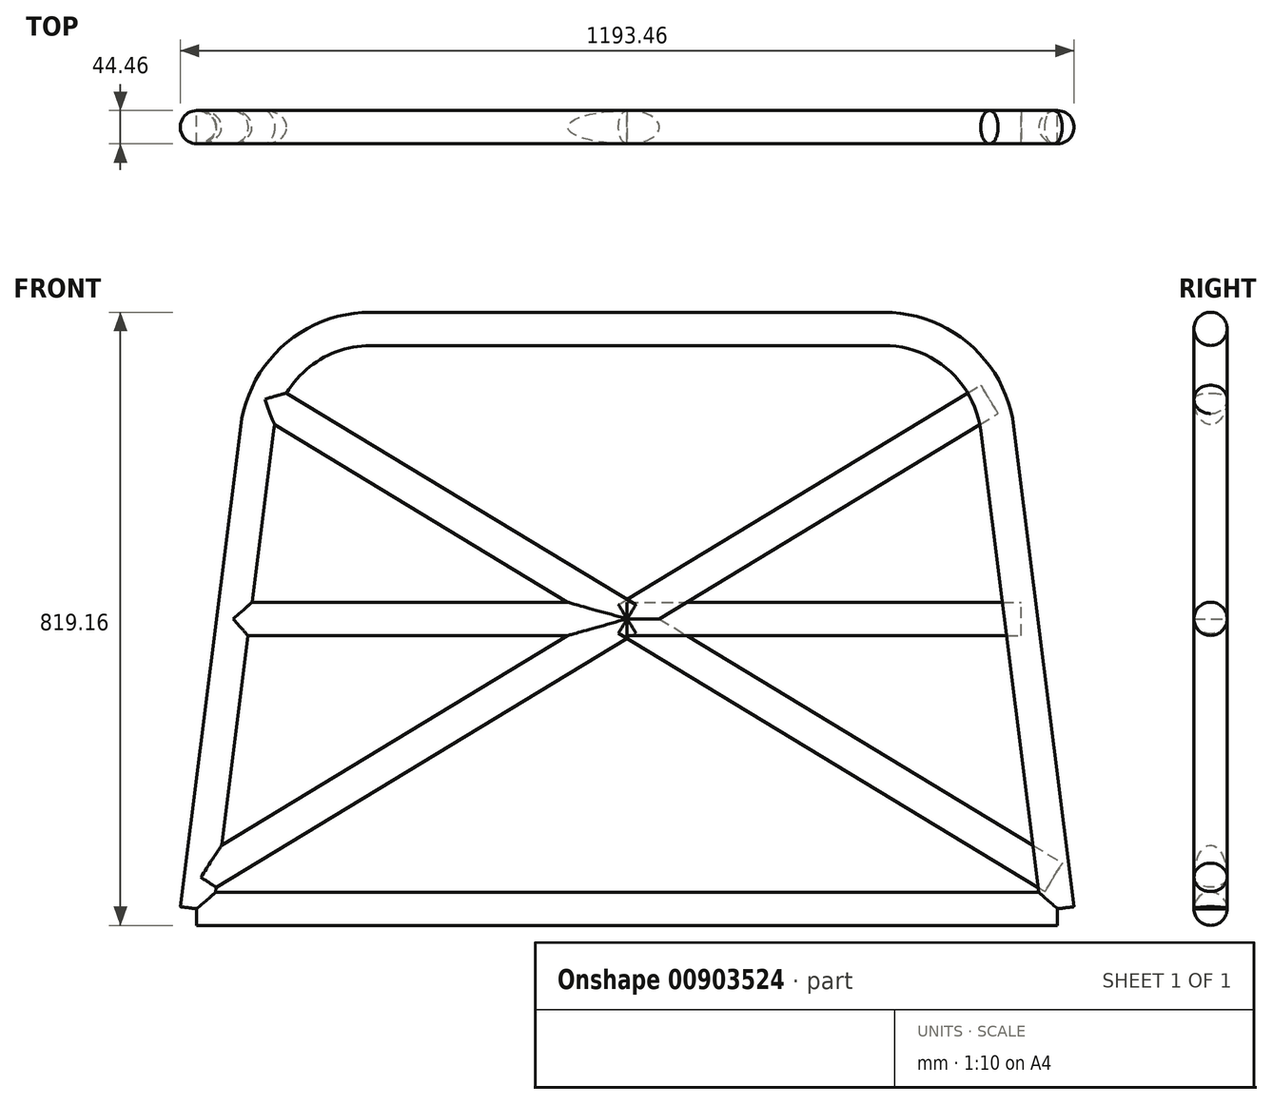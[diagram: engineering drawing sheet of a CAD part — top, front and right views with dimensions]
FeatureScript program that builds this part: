
annotation { "Feature Type Name" : "Feature", "Feature Type Description" : "" }
export const myFeature = defineFeature(function(context is Context, id is Id, definition is map)
    precondition{}
    {
        {
            var Q0;
            Q0=qCreatedBy(makeId("Front.planeOp"),FACE);
            var sketch = newSketch(context, id + "F0", { "sketchPlane" : qUnion([Q0])});
            skLineSegment(sketch, "E0", {"start": v(0, 0) * mm, "end": v(0, 387.35) * mm, "construction": true});
            skLineSegment(sketch, "E1", {"start": v(0, 0) * mm, "end": v(0, -387.35) * mm, "construction": true});
            skLineSegment(sketch, "E2", {"start": v(0, -387.35) * mm, "end": v(-552.45, -387.35) * mm});
            skCircle(sketch, "E3", {"center": v(-342.9, 234.95) * mm, "radius": 130.18 * mm});
            skLineSegment(sketch, "E4", {"start": v(-342.9, 365.12) * mm, "end": v(0, 365.12) * mm});
            skLineSegment(sketch, "E5", {"start": v(-342.9, 234.95) * mm, "end": v(-342.9, 365.12) * mm, "construction": true});
            skLineSegment(sketch, "E6", {"start": v(-552.45, -387.35) * mm, "end": v(-472.06, 251.21) * mm});
            skLineSegment(sketch, "E7", {"start": v(-552.45, -387.35) * mm, "end": v(-574.68, -387.35) * mm});
            skCircle(sketch, "E8", {"center": v(-574.68, -387.35) * mm, "radius": 22.23 * mm});
            skArc(sketch, "E9", {"start": v(-481.95, 172.58) * mm, "mid": v(-242.1, 120.65) * mm, "end": v(-263.65, 365.12) * mm});
            skLineSegment(sketch, "E10", {"start": v(-574.68, -387.35) * mm, "end": v(-494.11, 253.95) * mm});
            skLineSegment(sketch, "E11", {"start": v(0, 0) * mm, "end": v(-526.01, 0) * mm});
            skLineSegment(sketch, "E12", {"start": v(-552.45, -387.35) * mm, "end": v(-546.77, -342.27) * mm});
            skLineSegment(sketch, "E13", {"start": v(-571.9, -365.3) * mm, "end": v(-549.67, -365.3) * mm});
            skLineSegment(sketch, "E14", {"start": v(-549.67, -365.3) * mm, "end": v(-548.09, -352.7) * mm});
            skArc(sketch, "E15.trimOffspring", {"start": v(-342.9, 387.35) * mm, "mid": v(-443.72, 349.23) * mm, "end": v(-494.11, 253.95) * mm});
            skLineSegment(sketch, "E16", {"start": v(-342.9, 365.12) * mm, "end": v(-342.9, 387.35) * mm});
            skLineSegment(sketch, "E17", {"start": v(-342.9, 387.35) * mm, "end": v(0, 387.35) * mm});
            skPoint(sketch, "E18.orphan", {"position": v(0, 0) * mm});
            skCircle(sketch, "E19", {"center": v(0, 0) * mm, "radius": 22.23 * mm});
            skLineSegment(sketch, "E20", {"start": v(-548.09, -352.7) * mm, "end": v(-545.31, -330.65) * mm});
            skLineSegment(sketch, "E21", {"start": v(-545.31, -330.65) * mm, "end": v(0, 0) * mm});
            skLineSegment(sketch, "E22.MirrorCS", {"start": v(-483.7, 293.29) * mm, "end": v(0, 0) * mm});
            skLineSegment(sketch, "E23", {"start": v(-545.31, -330.65) * mm, "end": v(-569.39, -345.24) * mm});
            skSolve(sketch);
        }
        {
            var Q0;
            Q0=qCreatedBy(makeId("Right.planeOp"),FACE);
            var sketch = newSketch(context, id + "F1", { "sketchPlane" : qUnion([Q0])});
            skCircle(sketch, "E24", {"center": v(0, 0) * mm, "radius": 22.23 * mm});
            skCircle(sketch, "E25", {"center": v(0, 387.35) * mm, "radius": 22.23 * mm});
            skCircle(sketch, "E26", {"center": v(0, -387.35) * mm, "radius": 22.23 * mm});
            skSolve(sketch);
        }
        {
            var Q0;
            Q0=sQuery(id+"F0.wireOp",EDGE,"E22.MirrorCS");
            var Q1;
            Q1=sQuery(id+"F0.wireOp",VERTEX,"E18.orphan");
            cPlane(context, id + "F2", {"entities" : qUnion([Q0, Q1]), "cplaneType" : CPlaneType.LINE_POINT, "offset" : 25.4 * mm, "width" : 152.4 * mm, "height" : 152.4 * mm});
        }
        {
            var Q0;
            Q0=sQuery(id+"F0.wireOp",EDGE,"E21");
            var Q1;
            Q1=sQuery(id+"F0.wireOp",VERTEX,"E18.orphan");
            cPlane(context, id + "F3", {"entities" : qUnion([Q0, Q1]), "cplaneType" : CPlaneType.LINE_POINT, "offset" : 25.4 * mm, "width" : 152.4 * mm, "height" : 152.4 * mm});
        }
        {
            var Q0;
            Q0=qCreatedBy(id+"F2.planeOp",FACE);
            var sketch = newSketch(context, id + "F4", { "sketchPlane" : qUnion([Q0])});
            skCircle(sketch, "E27", {"center": v(0, 0) * mm, "radius": 22.23 * mm});
            skSolve(sketch);
        }
        {
            var Q0;
            Q0=qCreatedBy(id+"F3.planeOp",FACE);
            var sketch = newSketch(context, id + "F5", { "sketchPlane" : qUnion([Q0])});
            skCircle(sketch, "E28", {"center": v(0, 0) * mm, "radius": 22.23 * mm});
            skSolve(sketch);
        }
        {
            var Q0;
            Q0=makeQuery(id+"F5.imprint","IMPRINT",FACE,{"disambiguationData":[TD([[makeQuery(id+"F5.imprint","IMPRINT",EDGE,{"derivedFrom":sQuery(id+"F5.wireOp",EDGE,"E28")}),1.0]])]});
            var Q1;
            Q1=sQuery(id+"F0.wireOp",EDGE,"E21");
            var Q2;
            Q2=sQuery(id+"F0.wireOp",EDGE,"E23");
            sweep(context, id + "F6", {"profiles" : qUnion([Q0]), "path" : qUnion([Q1, Q2])});
        }
        {
            var Q0;
            Q0=makeQuery(id+"F4.imprint","IMPRINT",FACE,{"disambiguationData":[TD([[makeQuery(id+"F4.imprint","IMPRINT",EDGE,{"derivedFrom":sQuery(id+"F4.wireOp",EDGE,"E27")}),1.0]])]});
            var Q1;
            Q1=sQuery(id+"F0.wireOp",EDGE,"E22.MirrorCS");
            sweep(context, id + "F7", {"operationType" : NewBodyOperationType.ADD, "profiles" : qUnion([Q0]), "path" : qUnion([Q1])});
        }
        {
            var Q0;
            Q0=makeQuery(id+"F1.imprint","IMPRINT",FACE,{"disambiguationData":[TD([[makeQuery(id+"F1.imprint","IMPRINT",EDGE,{"derivedFrom":sQuery(id+"F1.wireOp",EDGE,"E24")}),1.0]])]});
            var Q1;
            Q1=sQuery(id+"F0.wireOp",EDGE,"E11");
            sweep(context, id + "F8", {"profiles" : qUnion([Q0]), "path" : qUnion([Q1])});
        }
        {
            var Q0;
            Q0=makeQuery(id+"F1.imprint","IMPRINT",FACE,{"disambiguationData":[TD([[makeQuery(id+"F1.imprint","IMPRINT",EDGE,{"derivedFrom":sQuery(id+"F1.wireOp",EDGE,"E25")}),1.0]])]});
            var Q1;
            Q1=sQuery(id+"F0.wireOp",EDGE,"E17");
            var Q2;
            Q2=sQuery(id+"F0.wireOp",EDGE,"E15.trimOffspring");
            var Q3;
            Q3=sQuery(id+"F0.wireOp",EDGE,"E10");
            sweep(context, id + "F9", {"profiles" : qUnion([Q0]), "path" : qUnion([Q1, Q2, Q3])});
        }
        {
            var Q0;
            Q0=makeQuery(id+"F1.imprint","IMPRINT",FACE,{"disambiguationData":[TD([[makeQuery(id+"F1.imprint","IMPRINT",EDGE,{"derivedFrom":sQuery(id+"F1.wireOp",EDGE,"E26")}),1.0]])]});
            var Q1;
            Q1=sQuery(id+"F0.wireOp",EDGE,"E2");
            var Q2;
            Q2=sQuery(id+"F0.wireOp",EDGE,"E7");
            sweep(context, id + "F10", {"operationType" : NewBodyOperationType.ADD, "profiles" : qUnion([Q0]), "path" : qUnion([Q1, Q2])});
        }
        {
            var Q0;
            Q0=makeQuery(id+"F8.opSweep","SWEPT_BODY",BODY,{"disambiguationData":[OSD([sQuery(id+"F0.wireOp",EDGE,"E11"),sQuery(id+"F1.wireOp",EDGE,"E24")])]});
            var Q1;
            Q1=makeQuery(id+"F6.opSweep","SWEPT_BODY",BODY,{"disambiguationData":[OSD([sQuery(id+"F0.wireOp",EDGE,"E23"),sQuery(id+"F5.wireOp",EDGE,"E28")])]});
            var Q2;
            Q2=makeQuery(id+"F9.opSweep","SWEPT_BODY",BODY,{"disambiguationData":[OSD([sQuery(id+"F0.wireOp",EDGE,"E10"),sQuery(id+"F1.wireOp",EDGE,"E25")])]});
            var Q3;
            Q3=qCreatedBy(makeId("Right.planeOp"),FACE);
            mirror(context, id + "F11", {"entities" : qUnion([Q0, Q1, Q2]), "mirrorPlane" : qUnion([Q3])});
        }
        {
            var Q0;
            Q0=makeQuery(id+"F1.imprint","IMPRINT",FACE,{"disambiguationData":[TD([[makeQuery(id+"F1.imprint","IMPRINT",EDGE,{"derivedFrom":sQuery(id+"F1.wireOp",EDGE,"E25")}),1.0]])]});
            var Q1;
            Q1=sQuery(id+"F0.wireOp",EDGE,"E17");
            var Q2;
            Q2=sQuery(id+"F0.wireOp",EDGE,"E15.trimOffspring");
            var Q3;
            Q3=sQuery(id+"F0.wireOp",EDGE,"E10");
            sweep(context, id + "F12", {"operationType" : NewBodyOperationType.ADD, "profiles" : qUnion([Q0]), "path" : qUnion([Q1, Q2, Q3])});
        }
    });
